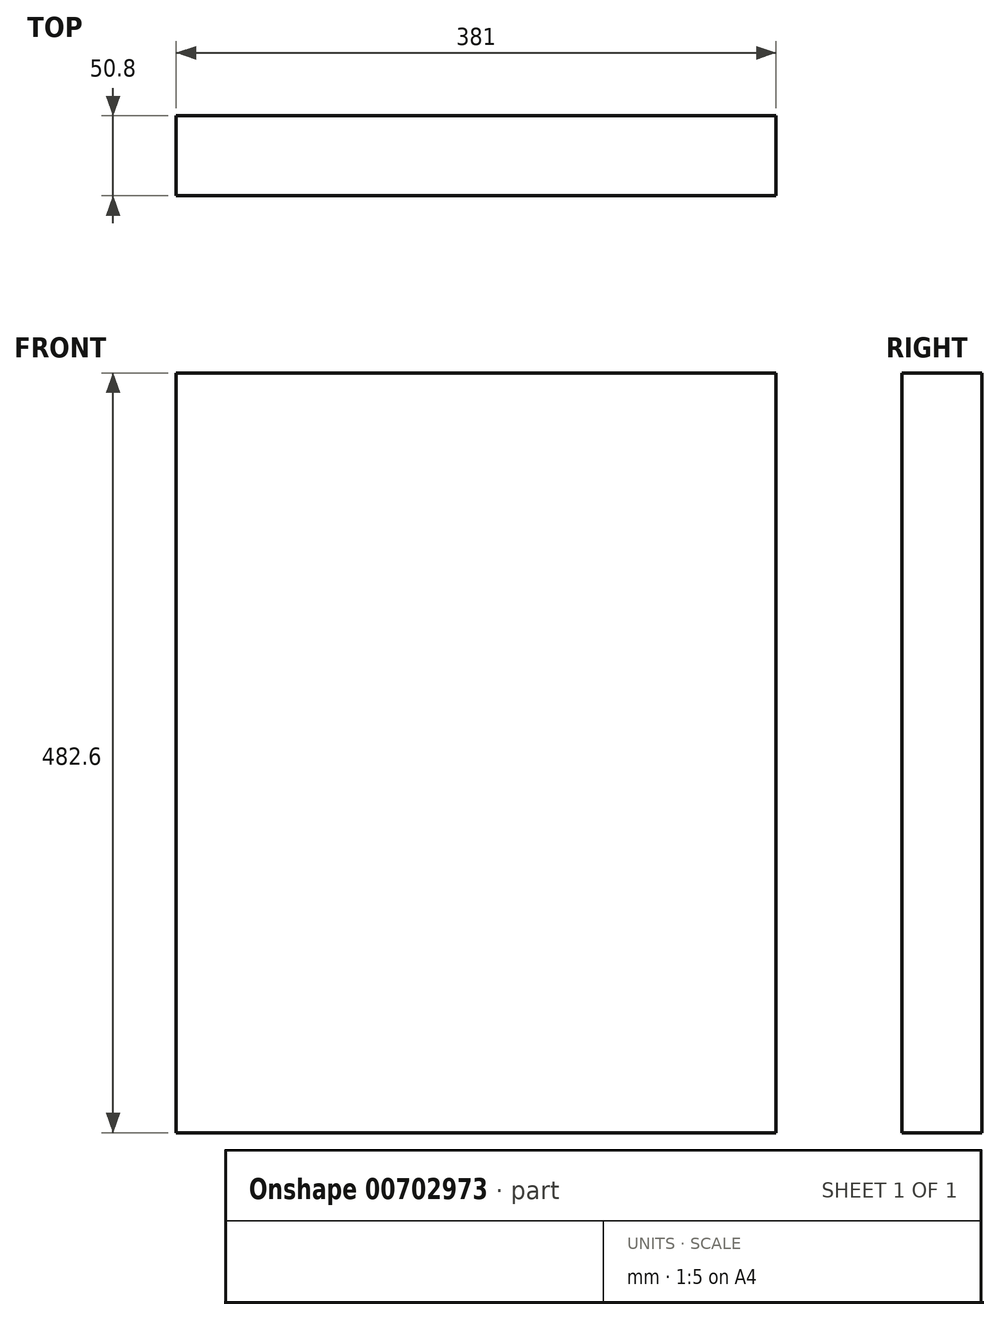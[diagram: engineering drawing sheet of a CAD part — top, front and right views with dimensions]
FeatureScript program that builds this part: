
annotation { "Feature Type Name" : "Feature", "Feature Type Description" : "" }
export const myFeature = defineFeature(function(context is Context, id is Id, definition is map)
    precondition{}
    {
        {
            var Q0;
            Q0=qCreatedBy(makeId("Front.planeOp"),FACE);
            var sketch = newSketch(context, id + "F0", { "sketchPlane" : qUnion([Q0])});
            skLineSegment(sketch, "E0.bottom", {"start": v(-189.8, 119.74) * mm, "end": v(191.2, 119.74) * mm});
            skLineSegment(sketch, "E0.top", {"start": v(-189.8, -362.86) * mm, "end": v(191.2, -362.86) * mm});
            skLineSegment(sketch, "E0.left", {"start": v(-189.8, 119.74) * mm, "end": v(-189.8, -362.86) * mm});
            skLineSegment(sketch, "E0.right", {"start": v(191.2, 119.74) * mm, "end": v(191.2, -362.86) * mm});
            skSolve(sketch);
        }
        {
            var Q0;
            Q0=makeQuery(id+"F0.imprint","IMPRINT",FACE,{"disambiguationData":[TD([[makeQuery(id+"F0.imprint","IMPRINT",EDGE,{"derivedFrom":sQuery(id+"F0.wireOp",EDGE,"E0.bottom")}),-1.0]])]});
            extrude(context, id + "F1", {"entities" : qUnion([Q0]), "depth" : 50.8 * mm, "offsetDistance" : 25.4 * mm});
        }
    });
